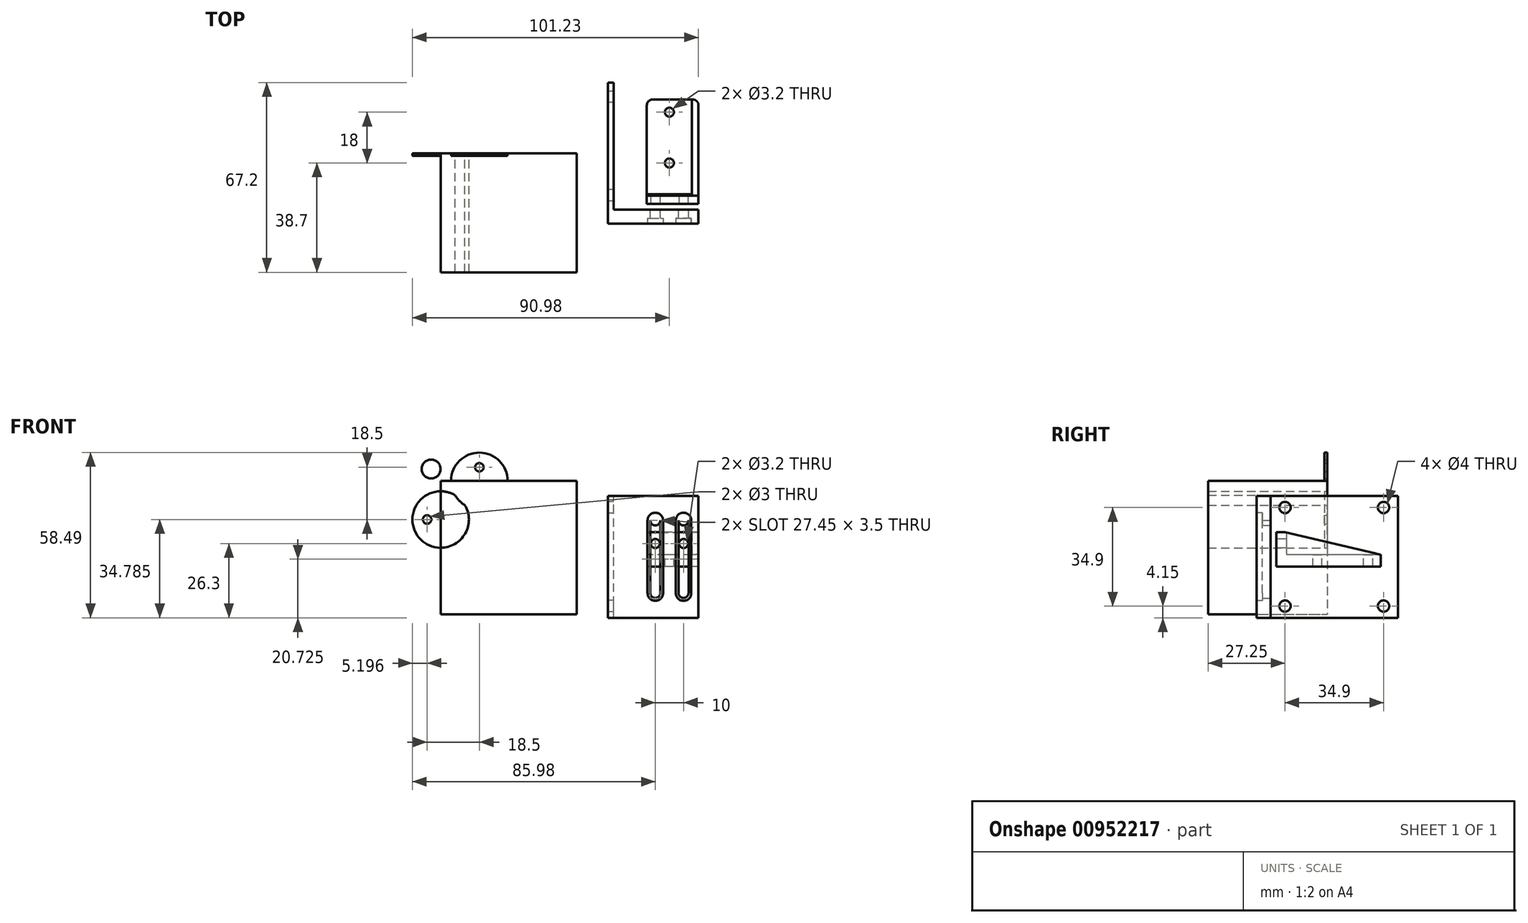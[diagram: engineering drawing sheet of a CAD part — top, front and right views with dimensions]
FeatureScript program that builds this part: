
annotation { "Feature Type Name" : "Feature", "Feature Type Description" : "" }
export const myFeature = defineFeature(function(context is Context, id is Id, definition is map)
    precondition{}
    {
        {
            var Q0;
            Q0=qCreatedBy(makeId("Right.planeOp"),FACE);
            var sketch = newSketch(context, id + "F0", { "sketchPlane" : qUnion([Q0])});
            skLineSegment(sketch, "E0.bottom", {"start": v(25, -21.6) * mm, "end": v(-25, -21.6) * mm});
            skLineSegment(sketch, "E0.top", {"start": v(25, 21.6) * mm, "end": v(-25, 21.6) * mm});
            skLineSegment(sketch, "E0.left", {"start": v(25, -21.6) * mm, "end": v(25, 21.6) * mm});
            skLineSegment(sketch, "E0.right", {"start": v(-25, -21.6) * mm, "end": v(-25, 21.6) * mm});
            skPoint(sketch, "E0.middle", {"position": v(0, 0) * mm});
            skLineSegment(sketch, "E1", {"start": v(-20, 0) * mm, "end": v(-20, -21.6) * mm});
            skLineSegment(sketch, "E2", {"start": v(-20, 0) * mm, "end": v(-20, 21.6) * mm});
            skCircle(sketch, "E3", {"center": v(-14.95, 17.45) * mm, "radius": 2 * mm});
            skCircle(sketch, "E4", {"center": v(19.95, 17.45) * mm, "radius": 2 * mm});
            skCircle(sketch, "E5", {"center": v(-14.95, -17.45) * mm, "radius": 2 * mm});
            skCircle(sketch, "E6", {"center": v(19.95, -17.45) * mm, "radius": 2 * mm});
            skPoint(sketch, "E7.endSnap0", {"position": v(-20, -10.8) * mm});
            skSolve(sketch);
        }
        {
            var Q0;
            {var subQ0=sQuery(id+"F0.wireOp",EDGE,"E0.left");Q0=makeQuery(id+"F0.imprint","IMPRINT",FACE,{"disambiguationData":[TD([[makeQuery(id+"F0.imprint","IMPRINT",EDGE,{"derivedFrom":subQ0}),1.0]])]});}
            extrude(context, id + "F1", {"entities" : qUnion([Q0]), "depth" : 2 * mm, "offsetDistance" : 25 * mm});
        }
        {
            var Q0;
            {var subQ0=sQuery(id+"F0.wireOp",EDGE,"E0.right");Q0=makeQuery(id+"F0.imprint","IMPRINT",FACE,{"disambiguationData":[TD([[makeQuery(id+"F0.imprint","IMPRINT",EDGE,{"derivedFrom":subQ0}),-1.0]])]});}
            extrude(context, id + "F2", {"entities" : qUnion([Q0]), "operationType" : NewBodyOperationType.ADD, "depth" : 32 * mm, "offsetDistance" : 25 * mm});
        }
        {
            var Q0;
            Q0=makeQuery(id+"F2.opExtrude","SWEPT_FACE",FACE,{"disambiguationData":[OSD([sQuery(id+"F0.wireOp",EDGE,"E1"),sQuery(id+"F0.wireOp",EDGE,"E2")])]});
            var sketch = newSketch(context, id + "F3", { "sketchPlane" : qUnion([Q0])});
            skCircle(sketch, "E8", {"center": v(-26.75, 12.85) * mm, "radius": 1.75 * mm});
            skCircle(sketch, "E9", {"center": v(-26.75, -12.85) * mm, "radius": 1.75 * mm});
            skCircle(sketch, "E10", {"center": v(-16.75, 12.85) * mm, "radius": 1.75 * mm});
            skCircle(sketch, "E11", {"center": v(-16.75, -12.85) * mm, "radius": 1.75 * mm});
            skLineSegment(sketch, "E12", {"start": v(-28.5, 12.85) * mm, "end": v(-28.5, -12.85) * mm});
            skLineSegment(sketch, "E13", {"start": v(-25, 12.85) * mm, "end": v(-25, -12.85) * mm});
            skLineSegment(sketch, "E14", {"start": v(-18.5, 12.85) * mm, "end": v(-18.5, -12.85) * mm});
            skLineSegment(sketch, "E15", {"start": v(-15, 12.85) * mm, "end": v(-15, -12.85) * mm});
            skSolve(sketch);
        }
        {
            var Q0;
            {var subQ0=sQuery(id+"F3.wireOp",EDGE,"E12");Q0=makeQuery(id+"F3.imprint","IMPRINT",FACE,{"disambiguationData":[TD([[makeQuery(id+"F3.imprint","IMPRINT",EDGE,{"derivedFrom":subQ0}),1.0]])]});}
            var Q1;
            {var subQ0=sQuery(id+"F3.wireOp",EDGE,"E8");var subQ2=makeQuery(id+"F3.imprint","IMPRINT",VERTEX,{"derivedFrom":subQ0});Q1=makeQuery(id+"F3.imprint","IMPRINT",FACE,{"disambiguationData":[TD([[makeQuery(id+"F3.imprint","IMPRINT",EDGE,{"disambiguationData":[TD([[subQ2,1.0]])],"derivedFrom":subQ0}),1.0]])]});}
            var Q2;
            {var subQ0=sQuery(id+"F3.wireOp",EDGE,"E9");var subQ1=makeQuery(id+"F3.imprint","INTERSECT",VERTEX,{"derivedFrom":[subQ0,sQuery(id+"F3.wireOp",EDGE,"E12")]});Q2=makeQuery(id+"F3.imprint","IMPRINT",FACE,{"disambiguationData":[TD([[makeQuery(id+"F3.imprint","IMPRINT",EDGE,{"disambiguationData":[TD([[subQ1,1.0]])],"derivedFrom":subQ0}),1.0]])]});}
            var Q3;
            {var subQ0=sQuery(id+"F3.wireOp",EDGE,"E14");Q3=makeQuery(id+"F3.imprint","IMPRINT",FACE,{"disambiguationData":[TD([[makeQuery(id+"F3.imprint","IMPRINT",EDGE,{"derivedFrom":subQ0}),1.0]])]});}
            var Q4;
            {var subQ0=sQuery(id+"F3.wireOp",EDGE,"E11");var subQ1=makeQuery(id+"F3.imprint","INTERSECT",VERTEX,{"derivedFrom":[subQ0,sQuery(id+"F3.wireOp",EDGE,"E14")]});Q4=makeQuery(id+"F3.imprint","IMPRINT",FACE,{"disambiguationData":[TD([[makeQuery(id+"F3.imprint","IMPRINT",EDGE,{"disambiguationData":[TD([[subQ1,1.0]])],"derivedFrom":subQ0}),1.0]])]});}
            var Q5;
            {var subQ0=sQuery(id+"F3.wireOp",EDGE,"E10");var subQ2=makeQuery(id+"F3.imprint","IMPRINT",VERTEX,{"derivedFrom":subQ0});Q5=makeQuery(id+"F3.imprint","IMPRINT",FACE,{"disambiguationData":[TD([[makeQuery(id+"F3.imprint","IMPRINT",EDGE,{"disambiguationData":[TD([[subQ2,1.0]])],"derivedFrom":subQ0}),1.0]])]});}
            extrude(context, id + "F4", {"entities" : qUnion([Q0, Q1, Q2, Q3, Q4, Q5]), "operationType" : NewBodyOperationType.REMOVE, "oppositeDirection" : true, "depth" : 25 * mm, "offsetDistance" : 25 * mm});
        }
        {
            var Q0;
            Q0=makeQuery(id+"F2.opExtrude","SWEPT_FACE",FACE,{"disambiguationData":[OSD([sQuery(id+"F0.wireOp",EDGE,"E0.right")])]});
            var sketch = newSketch(context, id + "F5", { "sketchPlane" : qUnion([Q0])});
            skArc(sketch, "E16.0", {"start": v(14, -12.85) * mm, "mid": v(16.75, -15.6) * mm, "end": v(19.5, -12.85) * mm});
            skLineSegment(sketch, "E16.1", {"start": v(14, -12.85) * mm, "end": v(14, 12.85) * mm});
            skArc(sketch, "E16.2", {"start": v(19.5, 12.85) * mm, "mid": v(16.75, 15.6) * mm, "end": v(14, 12.85) * mm});
            skLineSegment(sketch, "E16.3", {"start": v(19.5, -12.85) * mm, "end": v(19.5, 12.85) * mm});
            skLineSegment(sketch, "E17.0", {"start": v(29.5, -12.85) * mm, "end": v(29.5, 12.85) * mm});
            skArc(sketch, "E17.1", {"start": v(24, -12.85) * mm, "mid": v(26.75, -15.6) * mm, "end": v(29.5, -12.85) * mm});
            skLineSegment(sketch, "E17.2", {"start": v(24, -12.85) * mm, "end": v(24, 12.82) * mm});
            skArc(sketch, "E18.2", {"start": v(29.5, 12.85) * mm, "mid": v(26.74, 15.6) * mm, "end": v(24, 12.82) * mm});
            skSolve(sketch);
        }
        {
            var Q0;
            Q0=makeQuery(id+"F5.imprint","IMPRINT",FACE,{"disambiguationData":[TD([[makeQuery(id+"F5.imprint","IMPRINT",EDGE,{"derivedFrom":sQuery(id+"F5.wireOp",EDGE,"E16.0")}),1.0]])]});
            var Q1;
            Q1=makeQuery(id+"F5.imprint","IMPRINT",FACE,{"disambiguationData":[TD([[makeQuery(id+"F5.imprint","IMPRINT",EDGE,{"derivedFrom":sQuery(id+"F5.wireOp",EDGE,"E17.0")}),1.0]])]});
            extrude(context, id + "F6", {"entities" : qUnion([Q0, Q1]), "operationType" : NewBodyOperationType.REMOVE, "oppositeDirection" : true, "depth" : 2 * mm, "offsetDistance" : 25 * mm});
        }
        {
            var Q0;
            Q0=makeQuery(id+"F2.opExtrude","SWEPT_FACE",FACE,{"disambiguationData":[OSD([sQuery(id+"F0.wireOp",EDGE,"E1"),sQuery(id+"F0.wireOp",EDGE,"E2")])]});
            cPlane(context, id + "F7", {"entities" : qUnion([Q0]), "cplaneType" : CPlaneType.OFFSET, "offset" : 2 * mm, "width" : 150 * mm, "height" : 150 * mm});
        }
        {
            var Q0;
            Q0=qCreatedBy(id+"F7.planeOp",FACE);
            var sketch = newSketch(context, id + "F8", { "sketchPlane" : qUnion([Q0])});
            skLineSegment(sketch, "E19.bottom", {"start": v(-29.75, 8.7) * mm, "end": v(-13.75, 8.7) * mm});
            skLineSegment(sketch, "E19.top", {"start": v(-29.75, 0.7) * mm, "end": v(-13.75, 0.7) * mm});
            skLineSegment(sketch, "E19.left", {"start": v(-29.75, 8.7) * mm, "end": v(-29.75, 0.7) * mm});
            skLineSegment(sketch, "E19.right", {"start": v(-13.75, 8.7) * mm, "end": v(-13.75, 0.7) * mm});
            skLineSegment(sketch, "E20.top", {"start": v(-29.75, -3.5) * mm, "end": v(-13.75, -3.5) * mm});
            skLineSegment(sketch, "E20.left", {"start": v(-29.75, 0.7) * mm, "end": v(-29.75, -3.5) * mm});
            skLineSegment(sketch, "E20.right", {"start": v(-13.75, 0.7) * mm, "end": v(-13.75, -3.5) * mm});
            skCircle(sketch, "E21", {"center": v(-26.75, 4.7) * mm, "radius": 1.6 * mm});
            skCircle(sketch, "E22", {"center": v(-16.75, 4.7) * mm, "radius": 1.6 * mm});
            skLineSegment(sketch, "E23.bottom", {"start": v(-29.75, -3.5) * mm, "end": v(-32, -3.5) * mm});
            skLineSegment(sketch, "E23.top", {"start": v(-29.75, 8.7) * mm, "end": v(-32, 8.7) * mm});
            skLineSegment(sketch, "E23.left", {"start": v(-29.75, -3.5) * mm, "end": v(-29.75, 8.7) * mm});
            skLineSegment(sketch, "E23.right", {"start": v(-32, -3.5) * mm, "end": v(-32, 8.7) * mm});
            skSolve(sketch);
        }
        {
            var Q0;
            Q0=makeQuery(id+"F8.imprint","IMPRINT",FACE,{"disambiguationData":[TD([[makeQuery(id+"F8.imprint","IMPRINT",EDGE,{"derivedFrom":sQuery(id+"F8.wireOp",EDGE,"E20.top")}),1.0]])]});
            var Q1;
            {var subQ3=sQuery(id+"F8.wireOp",EDGE,"E23.bottom");Q1=makeQuery(id+"F8.imprint","IMPRINT",FACE,{"disambiguationData":[TD([[makeQuery(id+"F8.imprint","IMPRINT",EDGE,{"derivedFrom":subQ3}),-1.0]])]});}
            extrude(context, id + "F9", {"entities" : qUnion([Q0, Q1]), "depth" : 37 * mm, "offsetDistance" : 25 * mm});
        }
        {
            var Q0;
            {var subQ1=sQuery(id+"F8.wireOp",EDGE,"E19.left");Q0=makeQuery(id+"F8.imprint","IMPRINT",FACE,{"disambiguationData":[TD([[makeQuery(id+"F8.imprint","IMPRINT",EDGE,{"derivedFrom":subQ1}),1.0]])]});}
            var Q1;
            {var subQ1=sQuery(id+"F8.wireOp",EDGE,"E19.right");Q1=makeQuery(id+"F8.imprint","IMPRINT",FACE,{"disambiguationData":[TD([[makeQuery(id+"F8.imprint","IMPRINT",EDGE,{"derivedFrom":subQ1}),-1.0]])]});}
            extrude(context, id + "F10", {"entities" : qUnion([Q0, Q1]), "operationType" : NewBodyOperationType.ADD, "depth" : 3.5 * mm, "offsetDistance" : 25 * mm});
        }
        {
            var Q0;
            Q0=makeQuery(id+"F9.opExtrude","CAP_EDGE",EDGE,{"disambiguationData":[OSD([sQuery(id+"F8.wireOp",EDGE,"E23.top")])],"isStart":false});
            chamfer(context, id + "F11", {"entities" : qUnion([Q0]), "chamferType" : ChamferType.TWO_OFFSETS, "width1" : 8 * mm, "oppositeDirection" : false, "width2" : 34 * mm, "tangentPropagation" : true});
        }
        {
            var Q0;
            Q0=makeQuery(id+"F9.opExtrude","SWEPT_FACE",FACE,{"disambiguationData":[OSD([sQuery(id+"F8.wireOp",EDGE,"E19.top")])]});
            var sketch = newSketch(context, id + "F12", { "sketchPlane" : qUnion([Q0])});
            skCircle(sketch, "E24", {"center": v(21.75, -3.5) * mm, "radius": 1.6 * mm});
            skCircle(sketch, "E25", {"center": v(21.75, 14.5) * mm, "radius": 1.6 * mm});
            skSolve(sketch);
        }
        {
            var Q0;
            Q0=makeQuery(id+"F12.imprint","IMPRINT",FACE,{"disambiguationData":[TD([[makeQuery(id+"F12.imprint","IMPRINT",EDGE,{"derivedFrom":sQuery(id+"F12.wireOp",EDGE,"E24")}),1.0]])]});
            var Q1;
            Q1=makeQuery(id+"F12.imprint","IMPRINT",FACE,{"disambiguationData":[TD([[makeQuery(id+"F12.imprint","IMPRINT",EDGE,{"derivedFrom":sQuery(id+"F12.wireOp",EDGE,"E25")}),1.0]])]});
            extrude(context, id + "F13", {"entities" : qUnion([Q0, Q1]), "operationType" : NewBodyOperationType.REMOVE, "oppositeDirection" : true, "depth" : 5 * mm, "offsetDistance" : 25 * mm});
        }
        {
            var Q0;
            Q0=makeQuery(id+"F9.opExtrude","CAP_EDGE",EDGE,{"disambiguationData":[OSD([sQuery(id+"F8.wireOp",EDGE,"E20.right")])],"isStart":false});
            var Q1;
            Q1=makeQuery(id+"F9.opExtrude","CAP_EDGE",EDGE,{"disambiguationData":[OSD([sQuery(id+"F8.wireOp",EDGE,"E23.right")])],"isStart":false});
            fillet(context, id + "F14", {"entities" : qUnion([Q0, Q1]), "radius" : 2 * mm, "tangentPropagation" : true, "allowEdgeOverflow" : false});
        }
        {
            var Q0;
            Q0=qCreatedBy(makeId("Front.planeOp"),FACE);
            var sketch = newSketch(context, id + "F15", { "sketchPlane" : qUnion([Q0])});
            skLineSegment(sketch, "E26.bottom", {"start": v(-59.23, 26.89) * mm, "end": v(-11.05, 26.89) * mm});
            skLineSegment(sketch, "E26.top", {"start": v(-59.23, -20.31) * mm, "end": v(-11.05, -20.31) * mm});
            skLineSegment(sketch, "E26.left", {"start": v(-59.23, 26.89) * mm, "end": v(-59.23, -20.31) * mm});
            skLineSegment(sketch, "E26.right", {"start": v(-11.05, 26.89) * mm, "end": v(-11.05, -20.31) * mm});
            skCircle(sketch, "E27", {"center": v(-45.53, 26.89) * mm, "radius": 10 * mm});
            skCircle(sketch, "E28", {"center": v(-59.23, 13.19) * mm, "radius": 10 * mm});
            skCircle(sketch, "E29", {"center": v(-64.03, 13.19) * mm, "radius": 1.5 * mm});
            skCircle(sketch, "E30", {"center": v(-45.53, 31.69) * mm, "radius": 1.5 * mm});
            skCircle(sketch, "E31", {"center": v(-62.6, 31.08) * mm, "radius": 3.35 * mm});
            skSolve(sketch);
        }
        {
            var Q0;
            Q0=makeQuery(id+"F15.imprint","IMPRINT",FACE,{"disambiguationData":[TD([[makeQuery(id+"F15.imprint","IMPRINT",EDGE,{"derivedFrom":sQuery(id+"F15.wireOp",EDGE,"E26.bottom")}),-1.0]])]});
            var Q1;
            {var subQ0=sQuery(id+"F15.wireOp",EDGE,"E28");var subQ1=sQuery(id+"F15.wireOp",EDGE,"E26.left");var subQ2=makeQuery(id+"F15.imprint","INTERSECT",VERTEX,{"disambiguationData":[OD(0.0)],"derivedFrom":[subQ1,subQ0]});Q1=makeQuery(id+"F15.imprint","IMPRINT",FACE,{"disambiguationData":[TD([[makeQuery(id+"F15.imprint","IMPRINT",EDGE,{"disambiguationData":[TD([[subQ2,-1.0]])],"derivedFrom":subQ1}),1.0]])]});}
            var Q2;
            {var subQ0=sQuery(id+"F15.wireOp",EDGE,"E28");var subQ1=sQuery(id+"F15.wireOp",EDGE,"E27");var subQ2=makeQuery(id+"F15.imprint","INTERSECT",VERTEX,{"disambiguationData":[OD(0.0)],"derivedFrom":[subQ1,subQ0]});Q2=makeQuery(id+"F15.imprint","IMPRINT",FACE,{"disambiguationData":[TD([[makeQuery(id+"F15.imprint","IMPRINT",EDGE,{"disambiguationData":[TD([[subQ2,-1.0]])],"derivedFrom":subQ1}),1.0]])]});}
            var Q3;
            {var subQ1=sQuery(id+"F15.wireOp",EDGE,"E26.top");Q3=makeQuery(id+"F15.imprint","IMPRINT",FACE,{"disambiguationData":[TD([[makeQuery(id+"F15.imprint","IMPRINT",EDGE,{"derivedFrom":subQ1}),1.0]])]});}
            extrude(context, id + "F16", {"entities" : qUnion([Q0, Q1, Q2, Q3]), "depth" : 42.2 * mm, "offsetDistance" : 25 * mm});
        }
        {
            var Q0;
            Q0=makeQuery(id+"F15.imprint","IMPRINT",FACE,{"disambiguationData":[TD([[makeQuery(id+"F15.imprint","IMPRINT",EDGE,{"derivedFrom":sQuery(id+"F15.wireOp",EDGE,"E29")}),-1.0]])]});
            var Q1;
            Q1=makeQuery(id+"F15.imprint","IMPRINT",FACE,{"disambiguationData":[TD([[makeQuery(id+"F15.imprint","IMPRINT",EDGE,{"derivedFrom":sQuery(id+"F15.wireOp",EDGE,"E30")}),-1.0]])]});
            var Q2;
            Q2=makeQuery(id+"F15.imprint","IMPRINT",FACE,{"disambiguationData":[TD([[makeQuery(id+"F15.imprint","IMPRINT",EDGE,{"derivedFrom":sQuery(id+"F15.wireOp",EDGE,"E31")}),1.0]])]});
            extrude(context, id + "F17", {"entities" : qUnion([Q0, Q1, Q2]), "operationType" : NewBodyOperationType.ADD, "depth" : 1 * mm, "offsetDistance" : 25 * mm});
        }
    });
